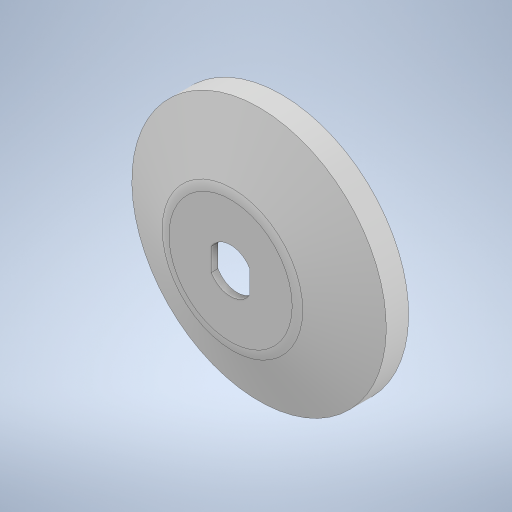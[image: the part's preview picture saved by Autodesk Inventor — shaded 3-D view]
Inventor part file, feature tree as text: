
AUTODESK INVENTOR PART (.ipt)
format: ipt  version: 2023 (Build 270158000, 158)  size: 320,000 bytes
history: native  units: mm
features: sketch x4, extrude x3, revolve x1, fillet x1, plane x1, pattern_circular x1
ambient origin geometry x8: Origin, YZ Plane, XZ Plane, XY Plane, X Axis, Y Axis, Z Axis, Center Point
bodies: Solid1 (feature_tree)
feature tree (11):
  extrude  "Extrusion1"  Depth=19.0mm
  revolve  "Revolution1"  [1 undecoded]
  fillet  "Fillet1"  Radius=7.0mm
  plane  "Work Plane2"
  extrude  "Extrusion2"  Depth=11.0mm
  sketch  "Sketch4"  dims[d11=30.0mm d12=90.0deg d13=10.0mm d14=9.0mm d19=61.0mm d20=6.0mm d21=0.0mm d22=1.0mm d23=0.0mm d24=0.0mm d25=45.0mm d26=18.0mm d27=100.0mm d28=360.0deg]
  extrude  "Extrusion3"  TaperAngle=90.0deg  [1 undecoded]
  pattern_circular  "Circular Pattern1"  [2 undecoded]
  sketch  "Sketch1"  dims[d0=22.0mm d1=19.0mm]
  sketch  "Sketch2"  dims[d2=65.0mm d3=3.3mm d4=0.0mm d8=7.0mm]
  sketch  "Sketch3"  dims[d9=25.0mm d10=11.0mm]
note: 4 required parameter values undecoded (feature->parameter linkage not recoverable at this tier; creation-order binding heuristic only, values carry confidence <= 0.55)